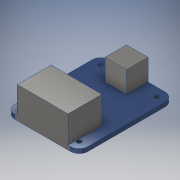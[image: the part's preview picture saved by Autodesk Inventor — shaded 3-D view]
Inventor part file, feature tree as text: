
AUTODESK INVENTOR PART (.ipt)
format: ipt  version: 2019 (Build 230136000, 136)  size: 156,672 bytes
history: native  units: in
note: dims shown in document units (in); Inventor stores cm internally (conversion verified against a paired STEP export)
features: extrude x3, sketch x3
ambient origin geometry x8: Origin, YZ Plane, XZ Plane, XY Plane, X Axis, Y Axis, Z Axis, Center Point
bodies: Solid1 (feature_tree)
feature tree (6):
  extrude  "Extrusion1"  Depth=1.1in
  extrude  "Extrusion2"  Depth=0.05in
  extrude  "Extrusion3"  Depth=0.05in
  sketch  "Sketch1"  dims[d0=0.85in d1=1.1in]
  sketch  "Sketch2"  dims[d2=0.1in d3=0.05in]
  sketch  "Sketch3"  dims[d4=0.05in d5=0.05in d6=0.05in d7=0.05in d8=0.0in d9=0.25in d10=0.25in d11=0.125in d12=0.25in d13=0.0in d14=0.5906in d15=0.3937in d16=0.315in d17=0.0in]
